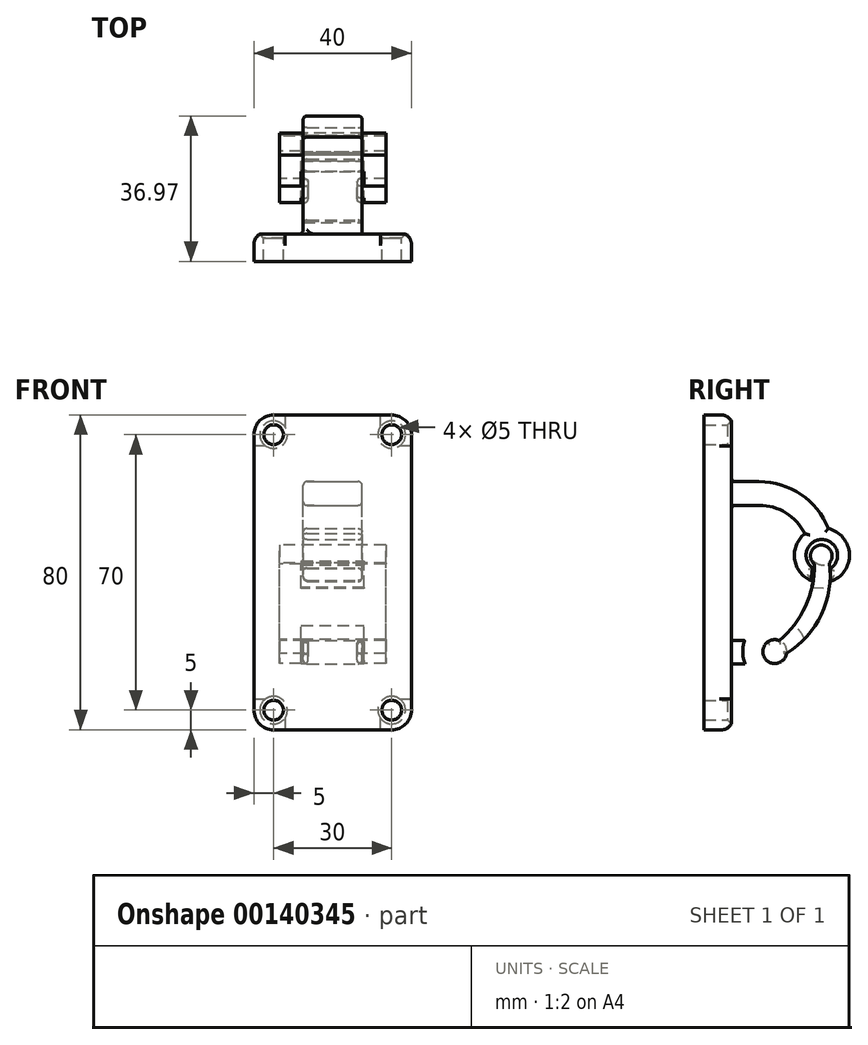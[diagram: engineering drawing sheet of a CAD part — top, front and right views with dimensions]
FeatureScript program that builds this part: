
annotation { "Feature Type Name" : "Feature", "Feature Type Description" : "" }
export const myFeature = defineFeature(function(context is Context, id is Id, definition is map)
    precondition{}
    {
        {
            var Q0;
            Q0=qCreatedBy(makeId("Front.planeOp"),FACE);
            var sketch = newSketch(context, id + "F0", { "sketchPlane" : qUnion([Q0])});
            skLineSegment(sketch, "E0.bottom", {"start": v(-15, 40) * mm, "end": v(15, 40) * mm});
            skLineSegment(sketch, "E0.top", {"start": v(-15, -40) * mm, "end": v(15, -40) * mm});
            skLineSegment(sketch, "E0.left", {"start": v(-20, 35) * mm, "end": v(-20, -35) * mm});
            skLineSegment(sketch, "E0.right", {"start": v(20, 35) * mm, "end": v(20, -35) * mm});
            skPoint(sketch, "E0.middle", {"position": v(0, 0) * mm});
            skLineSegment(sketch, "E1.bottom", {"start": v(-7.5, -17) * mm, "end": v(7.5, -17) * mm});
            skLineSegment(sketch, "E1.top", {"start": v(-7.5, -23) * mm, "end": v(7.5, -23) * mm});
            skLineSegment(sketch, "E1.left", {"start": v(-7.5, -17) * mm, "end": v(-7.5, -23) * mm});
            skLineSegment(sketch, "E1.right", {"start": v(7.5, -17) * mm, "end": v(7.5, -23) * mm});
            skPoint(sketch, "E1.middle", {"position": v(0, -20) * mm});
            skLineSegment(sketch, "E2.MirrorCS", {"start": v(-7.5, 17) * mm, "end": v(7.5, 17) * mm});
            skLineSegment(sketch, "E3.MirrorCS", {"start": v(-7.5, 17) * mm, "end": v(-7.5, 23) * mm});
            skLineSegment(sketch, "E4.MirrorCS", {"start": v(-7.5, 23) * mm, "end": v(7.5, 23) * mm});
            skLineSegment(sketch, "E5.MirrorCS", {"start": v(7.5, 17) * mm, "end": v(7.5, 23) * mm});
            skPoint(sketch, "E6.visualSharp", {"position": v(-20, 40) * mm});
            skArc(sketch, "E6.filletArc", {"start": v(-15, 40) * mm, "mid": v(-18.54, 38.54) * mm, "end": v(-20, 35) * mm});
            skPoint(sketch, "E7.visualSharp", {"position": v(20, 40) * mm});
            skArc(sketch, "E7.filletArc", {"start": v(20, 35) * mm, "mid": v(18.54, 38.54) * mm, "end": v(15, 40) * mm});
            skPoint(sketch, "E8.visualSharp", {"position": v(20, -40) * mm});
            skArc(sketch, "E8.filletArc", {"start": v(15, -40) * mm, "mid": v(18.54, -38.54) * mm, "end": v(20, -35) * mm});
            skPoint(sketch, "E9.visualSharp", {"position": v(-20, -40) * mm});
            skArc(sketch, "E9.filletArc", {"start": v(-20, -35) * mm, "mid": v(-18.54, -38.54) * mm, "end": v(-15, -40) * mm});
            skSolve(sketch);
        }
        {
            var Q0;
            Q0=makeQuery(id+"F0.imprint","IMPRINT",FACE,{"disambiguationData":[TD([[makeQuery(id+"F0.imprint","IMPRINT",EDGE,{"derivedFrom":sQuery(id+"F0.wireOp",EDGE,"E2.MirrorCS")}),1.0]])]});
            var Q1;
            Q1=makeQuery(id+"F0.imprint","IMPRINT",FACE,{"disambiguationData":[TD([[makeQuery(id+"F0.imprint","IMPRINT",EDGE,{"derivedFrom":sQuery(id+"F0.wireOp",EDGE,"E0.bottom")}),-1.0]])]});
            var Q2;
            Q2=makeQuery(id+"F0.imprint","IMPRINT",FACE,{"disambiguationData":[TD([[makeQuery(id+"F0.imprint","IMPRINT",EDGE,{"derivedFrom":sQuery(id+"F0.wireOp",EDGE,"E1.bottom")}),-1.0]])]});
            extrude(context, id + "F1", {"entities" : qUnion([Q0, Q1, Q2]), "oppositeDirection" : true, "depth" : 7 * mm});
        }
        {
            var Q0;
            Q0=qCreatedBy(makeId("Right.planeOp"),FACE);
            var sketch = newSketch(context, id + "F2", { "sketchPlane" : qUnion([Q0])});
            skLineSegment(sketch, "E10", {"start": v(-0.47, 23.07) * mm, "end": v(14, 23.07) * mm});
            skLineSegment(sketch, "E11", {"start": v(0, 17.07) * mm, "end": v(14, 17.07) * mm});
            skArc(sketch, "E12", {"start": v(14, 23.07) * mm, "mid": v(24.63, 19.8) * mm, "end": v(31.6, 11.16) * mm});
            skArc(sketch, "E13.0", {"start": v(14, 17.07) * mm, "mid": v(20.84, 15.11) * mm, "end": v(25.63, 9.84) * mm});
            skLineSegment(sketch, "E14", {"start": v(26.97, 4.3) * mm, "end": v(27.77, 4.32) * mm});
            skCircle(sketch, "E15", {"center": v(29.97, 4.35) * mm, "radius": 4 * mm});
            skLineSegment(sketch, "E16", {"start": v(0.13, -17.33) * mm, "end": v(11.71, -17.33) * mm});
            skLineSegment(sketch, "E17", {"start": v(0, -23.2) * mm, "end": v(11.71, -23.2) * mm});
            skArc(sketch, "E18", {"start": v(11.71, -23.2) * mm, "mid": v(25.07, -20.26) * mm, "end": v(11.71, -17.33) * mm});
            skCircle(sketch, "E19", {"center": v(18.07, -20.26) * mm, "radius": 4 * mm});
            skLineSegment(sketch, "E20.trimOffspring", {"start": v(18, -17.33) * mm, "end": v(18.13, -17.33) * mm});
            skLineSegment(sketch, "E21.trimOffspring", {"start": v(32.88, 4.4) * mm, "end": v(32.97, 4.4) * mm});
            skCircle(sketch, "E22.converted", {"center": v(29.97, 4.35) * mm, "radius": 7 * mm});
            skPoint(sketch, "E23.orphan", {"position": v(0, 23.07) * mm});
            skLineSegment(sketch, "E24", {"start": v(0, 23.07) * mm, "end": v(0, 17.07) * mm});
            skLineSegment(sketch, "E25", {"start": v(0.13, -17.33) * mm, "end": v(0, -23.2) * mm});
            skSolve(sketch);
        }
        {
            var Q0;
            Q0=makeQuery(id+"F1.opExtrude","CAP_FACE",FACE,{"disambiguationData":[OSD([sQuery(id+"F0.wireOp",EDGE,"E0.bottom"),sQuery(id+"F0.wireOp",EDGE,"E0.top"),sQuery(id+"F0.wireOp",EDGE,"E0.left"),sQuery(id+"F0.wireOp",EDGE,"E0.right"),sQuery(id+"F0.wireOp",EDGE,"E6.filletArc"),sQuery(id+"F0.wireOp",EDGE,"E7.filletArc"),sQuery(id+"F0.wireOp",EDGE,"E8.filletArc"),sQuery(id+"F0.wireOp",EDGE,"E9.filletArc")])],"isStart":false});
            var sketch = newSketch(context, id + "F3", { "sketchPlane" : qUnion([Q0])});
            skPoint(sketch, "E26", {"position": v(-15, 35) * mm});
            skPoint(sketch, "E27", {"position": v(15, 35) * mm});
            skPoint(sketch, "E28", {"position": v(15, -35) * mm});
            skPoint(sketch, "E29", {"position": v(-15, -35) * mm});
            skSolve(sketch);
        }
        {
            var Q0;
            Q0=sQuery(id+"F3.wireOp",VERTEX,"E27");
            var Q1;
            Q1=sQuery(id+"F3.wireOp",VERTEX,"E26");
            var Q2;
            Q2=sQuery(id+"F3.wireOp",VERTEX,"E28");
            var Q3;
            Q3=sQuery(id+"F3.wireOp",VERTEX,"E29");
            var Q4;
            Q4=makeQuery(id+"F1.opExtrude","SWEPT_BODY",BODY,{"disambiguationData":[OSD([sQuery(id+"F0.wireOp",EDGE,"E0.bottom"),sQuery(id+"F0.wireOp",EDGE,"E0.top"),sQuery(id+"F0.wireOp",EDGE,"E0.left"),sQuery(id+"F0.wireOp",EDGE,"E0.right"),sQuery(id+"F0.wireOp",EDGE,"E6.filletArc"),sQuery(id+"F0.wireOp",EDGE,"E7.filletArc"),sQuery(id+"F0.wireOp",EDGE,"E8.filletArc"),sQuery(id+"F0.wireOp",EDGE,"E9.filletArc")])]});
            hole(context, id + "F4", {"style" : HoleStyle.C_SINK, "endStyle" : HoleEndStyle.THROUGH, "holeDiameter" : 5 * mm, "cSinkDiameter" : 7 * mm, "cSinkAngle" : 90 * degree, "locations" : qUnion([Q0, Q1, Q2, Q3]), "scope" : qUnion([Q4]), "isTappedThrough" : true});
        }
        {
            var Q0;
            Q0=qCreatedBy(makeId("Right.planeOp"),FACE);
            var sketch = newSketch(context, id + "F5", { "sketchPlane" : qUnion([Q0])});
            skArc(sketch, "E30", {"start": v(27.88, 2.9) * mm, "mid": v(29.88, 1.9) * mm, "end": v(32.06, 2.38) * mm});
            skLineSegment(sketch, "E31", {"start": v(27.88, 2.9) * mm, "end": v(26.94, -3.78) * mm});
            skLineSegment(sketch, "E32", {"start": v(26.94, -3.78) * mm, "end": v(32.21, -4.12) * mm});
            skLineSegment(sketch, "E33", {"start": v(32.21, -4.12) * mm, "end": v(32.06, 2.38) * mm});
            skSolve(sketch);
        }
        {
            var Q0;
            Q0=makeQuery(id+"F1.opExtrude","CAP_EDGE",EDGE,{"disambiguationData":[OSD([sQuery(id+"F0.wireOp",EDGE,"E0.bottom")])],"isStart":false});
            fillet(context, id + "F6", {"entities" : qUnion([Q0]), "radius" : 3 * mm, "tangentPropagation" : true, "allowEdgeOverflow" : false});
        }
        {
            var Q0;
            {var subQ1=sQuery(id+"F2.wireOp",EDGE,"E16");Q0=makeQuery(id+"F2.imprint","IMPRINT",FACE,{"disambiguationData":[TD([[makeQuery(id+"F2.imprint","IMPRINT",EDGE,{"derivedFrom":subQ1}),-1.0]])]});}
            var Q1;
            {var subQ0=sQuery(id+"F2.wireOp",EDGE,"C32lH3EJ-jwJ5-gCcF-TI2y-UIbqiRQANIjS");var subQ1=sQuery(id+"F2.wireOp",EDGE,"E18");var subQ2=makeQuery(id+"F2.imprint","INTERSECT",VERTEX,{"derivedFrom":[subQ1,subQ0]});Q1=makeQuery(id+"F2.imprint","IMPRINT",FACE,{"disambiguationData":[TD([[makeQuery(id+"F2.imprint","IMPRINT",EDGE,{"disambiguationData":[TD([[subQ2,-1.0]])],"derivedFrom":subQ1}),1.0]])]});}
            var Q2;
            Q2=makeQuery(id+"F2.imprint","IMPRINT",FACE,{"disambiguationData":[TD([[makeQuery(id+"F2.imprint","IMPRINT",EDGE,{"derivedFrom":sQuery(id+"F2.wireOp",EDGE,"E11")}),1.0]])]});
            var Q3;
            {var subQ3=sQuery(id+"F2.wireOp",EDGE,"E15");var subQ7=sQuery(id+"F2.wireOp",EDGE,"lnQvz7nI-boOK-pGjN-hhzM-7sdql3FDUyVG");var subQ9=makeQuery(id+"F2.imprint","INTERSECT",VERTEX,{"derivedFrom":[subQ3,subQ7]});Q3=makeQuery(id+"F2.imprint","IMPRINT",FACE,{"disambiguationData":[TD([[makeQuery(id+"F2.imprint","IMPRINT",EDGE,{"disambiguationData":[TD([[subQ9,1.0]])],"derivedFrom":subQ3}),-1.0]])]});}
            var Q4;
            {var subQ0=sQuery(id+"F2.wireOp",EDGE,"lnQvz7nI-boOK-pGjN-hhzM-7sdql3FDUyVG");var subQ1=sQuery(id+"F2.wireOp",EDGE,"E15");var subQ2=makeQuery(id+"F2.imprint","INTERSECT",VERTEX,{"derivedFrom":[subQ1,subQ0]});Q4=makeQuery(id+"F2.imprint","IMPRINT",FACE,{"disambiguationData":[TD([[makeQuery(id+"F2.imprint","IMPRINT",EDGE,{"disambiguationData":[TD([[subQ2,-1.0]])],"derivedFrom":subQ1}),-1.0]])]});}
            var Q5;
            Q5=makeQuery(id+"F2.imprint","IMPRINT",FACE,{"disambiguationData":[TD([[makeQuery(id+"F2.imprint","IMPRINT",EDGE,{"derivedFrom":sQuery(id+"F2.wireOp",EDGE,"E15")}),-1.0]])]});
            extrude(context, id + "F7", {"entities" : qUnion([Q0, Q1, Q2, Q3, Q4, Q5]), "operationType" : NewBodyOperationType.ADD, "endBound" : BoundingType.SYMMETRIC, "oppositeDirection" : true, "depth" : 15 * mm});
        }
        {
            var Q0;
            Q0=qCreatedBy(makeId("Right.planeOp"),FACE);
            var sketch = newSketch(context, id + "F8", { "sketchPlane" : qUnion([Q0])});
            skCircle(sketch, "E34", {"center": v(29.82, 4.2) * mm, "radius": 2.74 * mm});
            skCircle(sketch, "E35", {"center": v(18, -20.12) * mm, "radius": 3.04 * mm});
            skArc(sketch, "E36", {"start": v(19.18, -17.32) * mm, "mid": v(25.8, -8.6) * mm, "end": v(28.05, 2.11) * mm});
            skArc(sketch, "E37", {"start": v(21, -20.6) * mm, "mid": v(29.84, -10.7) * mm, "end": v(31.89, 2.41) * mm});
            skSolve(sketch);
        }
        {
            var Q0;
            {var subQ0=sQuery(id+"F8.wireOp",EDGE,"E36");Q0=makeQuery(id+"F8.imprint","IMPRINT",FACE,{"disambiguationData":[TD([[makeQuery(id+"F8.imprint","IMPRINT",EDGE,{"derivedFrom":subQ0}),-1.0]])]});}
            var Q1;
            {var subQ0=sQuery(id+"F8.wireOp",EDGE,"E34");var subQ1=makeQuery(id+"F8.imprint","INTERSECT",VERTEX,{"derivedFrom":[subQ0,sQuery(id+"F8.wireOp",EDGE,"E36")]});Q1=makeQuery(id+"F8.imprint","IMPRINT",FACE,{"disambiguationData":[TD([[makeQuery(id+"F8.imprint","IMPRINT",EDGE,{"disambiguationData":[TD([[subQ1,-1.0]])],"derivedFrom":subQ0}),1.0]])]});}
            var Q2;
            {var subQ0=sQuery(id+"F8.wireOp",EDGE,"E35");var subQ1=makeQuery(id+"F8.imprint","INTERSECT",VERTEX,{"derivedFrom":[subQ0,sQuery(id+"F8.wireOp",EDGE,"E36")]});Q2=makeQuery(id+"F8.imprint","IMPRINT",FACE,{"disambiguationData":[TD([[makeQuery(id+"F8.imprint","IMPRINT",EDGE,{"disambiguationData":[TD([[subQ1,-1.0]])],"derivedFrom":subQ0}),1.0]])]});}
            extrude(context, id + "F9", {"entities" : qUnion([Q0, Q1, Q2]), "endBound" : BoundingType.SYMMETRIC, "depth" : 27 * mm});
        }
        {
            var Q0;
            Q0 = qSketchRegion(id + "F5", true);
            extrude(context, id + "F10", {"entities" : qUnion([Q0]), "operationType" : NewBodyOperationType.REMOVE, "endBound" : BoundingType.SYMMETRIC, "oppositeDirection" : true, "depth" : 16 * mm});
        }
        {
            var Q0;
            Q0=qCreatedBy(makeId("Right.planeOp"),FACE);
            var sketch = newSketch(context, id + "F11", { "sketchPlane" : qUnion([Q0])});
            skCircle(sketch, "E38", {"center": v(18.03, -20.08) * mm, "radius": 3.02 * mm});
            skPoint(sketch, "E38.first.point", {"position": v(17.46, -17.1) * mm});
            skPoint(sketch, "E38.second.point", {"position": v(16.18, -22.47) * mm});
            skPoint(sketch, "E38.third.point", {"position": v(20.02, -22.35) * mm});
            skCircle(sketch, "E39", {"center": v(18.03, -20.08) * mm, "radius": 8.17 * mm});
            skSolve(sketch);
        }
        {
            var Q0;
            Q0=makeQuery(id+"F11.imprint","IMPRINT",FACE,{"disambiguationData":[TD([[makeQuery(id+"F11.imprint","IMPRINT",EDGE,{"derivedFrom":sQuery(id+"F11.wireOp",EDGE,"E38")}),-1.0]])]});
            extrude(context, id + "F12", {"entities" : qUnion([Q0]), "operationType" : NewBodyOperationType.REMOVE, "endBound" : BoundingType.SYMMETRIC, "oppositeDirection" : true, "depth" : 16 * mm});
        }
        {
            var Q0;
            Q0=makeQuery(id+"F11.imprint","IMPRINT",FACE,{"disambiguationData":[TD([[makeQuery(id+"F11.imprint","IMPRINT",EDGE,{"derivedFrom":sQuery(id+"F11.wireOp",EDGE,"E38")}),1.0]])]});
            extrude(context, id + "F13", {"entities" : qUnion([Q0]), "operationType" : NewBodyOperationType.REMOVE, "endBound" : BoundingType.SYMMETRIC, "depth" : 12.5 * mm});
        }
        {
            var Q0;
            Q0=makeQuery(id+"F7.opExtrude","CAP_EDGE",EDGE,{"disambiguationData":[OSD([sQuery(id+"F2.wireOp",EDGE,"E10")])],"isStart":true});
            var Q1;
            Q1=makeQuery(id+"F7.opExtrude","CAP_EDGE",EDGE,{"disambiguationData":[OSD([sQuery(id+"F2.wireOp",EDGE,"E12")])],"isStart":true});
            var Q2;
            Q2=makeQuery(id+"F7.opExtrude","CAP_EDGE",EDGE,{"disambiguationData":[OSD([sQuery(id+"F2.wireOp",EDGE,"E22.converted")])],"isStart":true});
            var Q3;
            Q3=makeQuery(id+"F7.opExtrude","CAP_EDGE",EDGE,{"disambiguationData":[OSD([sQuery(id+"F2.wireOp",EDGE,"E13.0")])],"isStart":true});
            var Q4;
            Q4=makeQuery(id+"F7.opExtrude","CAP_EDGE",EDGE,{"disambiguationData":[OSD([sQuery(id+"F2.wireOp",EDGE,"E11")])],"isStart":true});
            var Q5;
            Q5=makeQuery(id+"F7.opExtrude","CAP_EDGE",EDGE,{"disambiguationData":[OSD([sQuery(id+"F2.wireOp",EDGE,"E18")])],"isStart":true});
            var Q6;
            Q6=makeQuery(id+"F7.opExtrude","CAP_EDGE",EDGE,{"disambiguationData":[OSD([sQuery(id+"F2.wireOp",EDGE,"E17")])],"isStart":true});
            var Q7;
            Q7=makeQuery(id+"F7.opExtrude","CAP_EDGE",EDGE,{"disambiguationData":[OSD([sQuery(id+"F2.wireOp",EDGE,"E16")])],"isStart":true});
            var Q8;
            Q8=makeQuery(id+"F7.opExtrude","CAP_EDGE",EDGE,{"disambiguationData":[OSD([sQuery(id+"F2.wireOp",EDGE,"E15")])],"isStart":true});
            var Q9;
            Q9=makeQuery(id+"F7.opExtrude","CAP_EDGE",EDGE,{"disambiguationData":[OSD([sQuery(id+"F2.wireOp",EDGE,"E19")])],"isStart":true});
            fillet(context, id + "F14", {"entities" : qUnion([Q0, Q1, Q2, Q3, Q4, Q5, Q6, Q7, Q8, Q9]), "radius" : 1 * mm, "tangentPropagation" : true, "allowEdgeOverflow" : false});
        }
        {
            var Q0;
            Q0=makeQuery(id+"F7.opExtrude","CAP_FACE",FACE,{"disambiguationData":[OSD([sQuery(id+"F2.wireOp",EDGE,"E10"),sQuery(id+"F2.wireOp",EDGE,"E11"),sQuery(id+"F2.wireOp",EDGE,"E12"),sQuery(id+"F2.wireOp",EDGE,"E13.0"),sQuery(id+"F2.wireOp",EDGE,"E15"),sQuery(id+"F2.wireOp",EDGE,"E22.converted"),sQuery(id+"F2.wireOp",EDGE,"E24")])],"isStart":false});
            var Q1;
            Q1=makeQuery(id+"F7.opExtrude","CAP_EDGE",EDGE,{"disambiguationData":[OSD([sQuery(id+"F2.wireOp",EDGE,"E16")])],"isStart":false});
            var Q2;
            Q2=makeQuery(id+"F7.opExtrude","CAP_EDGE",EDGE,{"disambiguationData":[OSD([sQuery(id+"F2.wireOp",EDGE,"E17")])],"isStart":false});
            var Q3;
            Q3=makeQuery(id+"F7.opExtrude","CAP_EDGE",EDGE,{"disambiguationData":[OSD([sQuery(id+"F2.wireOp",EDGE,"E18")])],"isStart":false});
            var Q4;
            Q4=makeQuery(id+"F7.opExtrude","CAP_EDGE",EDGE,{"disambiguationData":[OSD([sQuery(id+"F2.wireOp",EDGE,"E19")])],"isStart":false});
            fillet(context, id + "F15", {"entities" : qUnion([Q0, Q1, Q2, Q3, Q4]), "radius" : 1 * mm, "tangentPropagation" : true, "allowEdgeOverflow" : false});
        }
        {
            var Q0;
            Q0=makeQuery(id+"F13.boolean.opBoolean","COPY",FACE,{"derivedFrom":makeQuery(id+"F13.opExtrude","CAP_FACE",FACE,{"disambiguationData":[OSD([sQuery(id+"F11.wireOp",EDGE,"E38")])],"isStart":true})});
            var Q1;
            Q1=makeQuery(id+"F13.boolean.opBoolean","COPY",FACE,{"derivedFrom":makeQuery(id+"F13.opExtrude","CAP_FACE",FACE,{"disambiguationData":[OSD([sQuery(id+"F11.wireOp",EDGE,"E38")])],"isStart":false})});
            fillet(context, id + "F16", {"entities" : qUnion([Q0, Q1]), "radius" : .8 * mm, "tangentPropagation" : true, "allowEdgeOverflow" : false});
        }
    });
